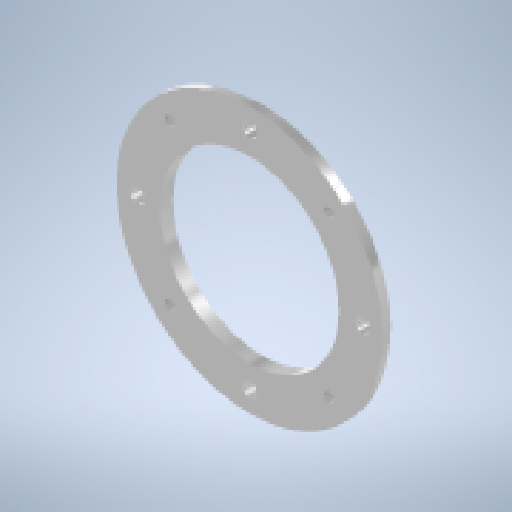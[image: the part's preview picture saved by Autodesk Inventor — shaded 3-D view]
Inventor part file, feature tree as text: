
AUTODESK INVENTOR PART (.ipt)
format: ipt  version: 2024 (Build 280153000, 153)  size: 186,880 bytes
history: native  units: mm
features: sketch x5, extrude x3, hole x2, pattern_circular x2, other x1, thread x1
ambient origin geometry x8: Origin, YZ Plane, XZ Plane, XY Plane, X Axis, Y Axis, Z Axis, Center Point
bodies: Body1 (feature_tree)
feature tree (14):
  other  "ソリッド1"
  extrude  "押し出し1"  Depth=100.0mm
  extrude  "押し出し2"  Depth=2.5mm TaperAngle=0.0deg
  hole  "穴1"  [1 undecoded]
  pattern_circular  "円形状パターン1"  [2 undecoded]
  hole  "穴2"  [1 undecoded]
  thread  "ねじ1"
  pattern_circular  "円形状パターン2"  Count=4 Angle=360.0deg
  extrude  "押し出し3"  TaperAngle=45.0deg  [1 undecoded]
  sketch  "スケッチ1"
  sketch  "スケッチ2"
  sketch  "スケッチ3"
  sketch  "スケッチ4"
  sketch  "スケッチ5"
note: 5 required parameter values undecoded (feature->parameter linkage not recoverable at this tier; creation-order binding heuristic only, values carry confidence <= 0.55)
